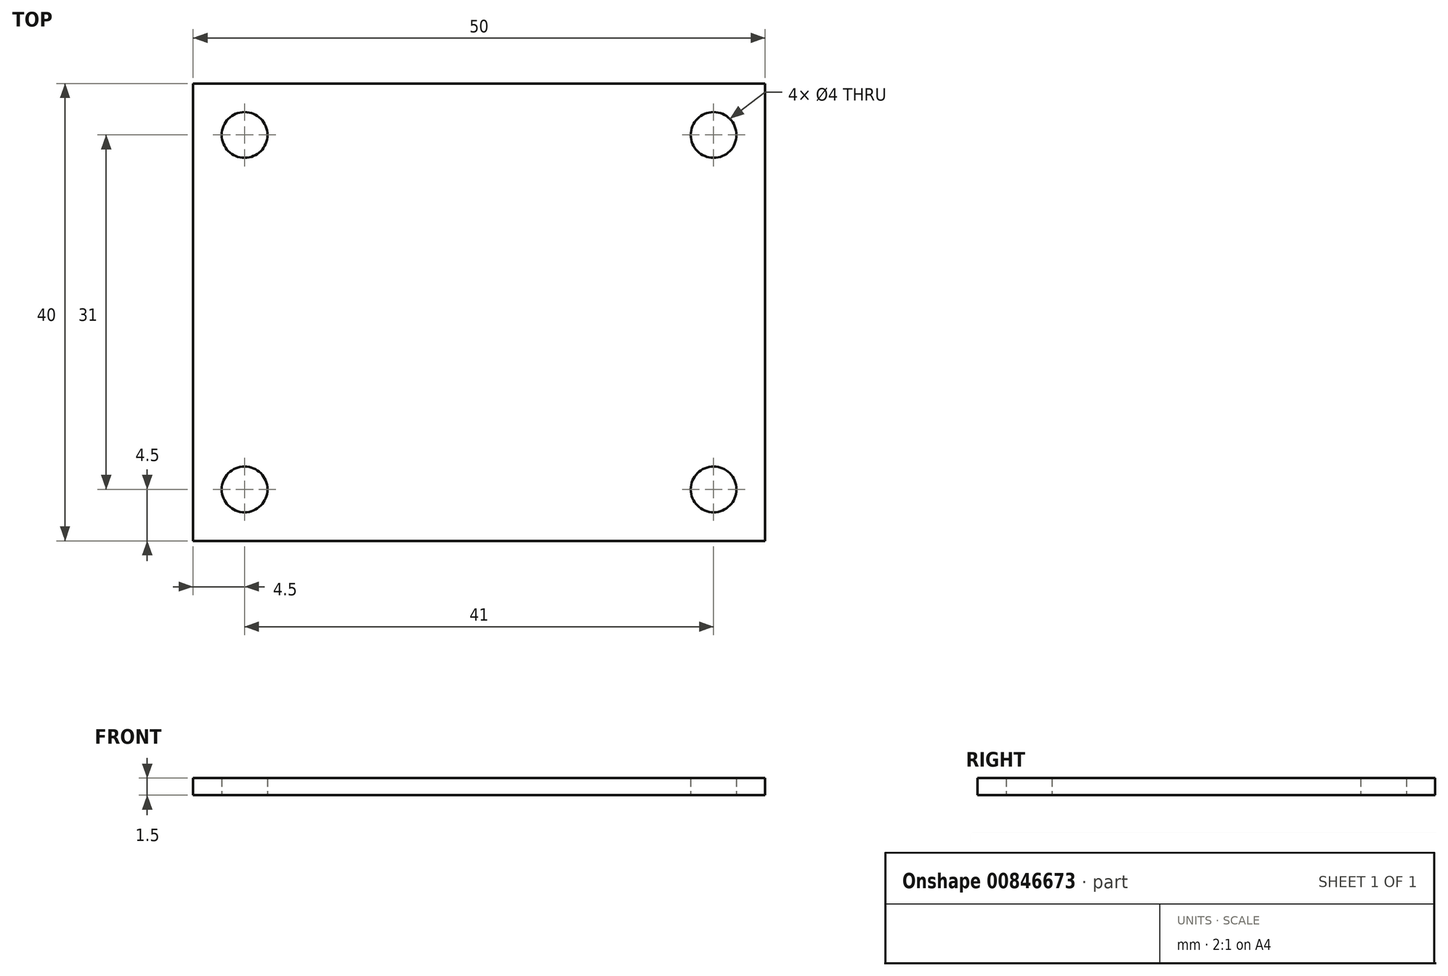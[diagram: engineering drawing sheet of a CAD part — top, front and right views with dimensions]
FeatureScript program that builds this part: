
annotation { "Feature Type Name" : "Feature", "Feature Type Description" : "" }
export const myFeature = defineFeature(function(context is Context, id is Id, definition is map)
    precondition{}
    {
        {
            var Q0;
            Q0=qCreatedBy(makeId("Top.planeOp"),FACE);
            var sketch = newSketch(context, id + "F0", { "sketchPlane" : qUnion([Q0])});
            skLineSegment(sketch, "E0.bottom", {"start": v(-25, 20) * mm, "end": v(25, 20) * mm});
            skLineSegment(sketch, "E0.top", {"start": v(-25, -20) * mm, "end": v(25, -20) * mm});
            skLineSegment(sketch, "E0.left", {"start": v(-25, 20) * mm, "end": v(-25, -20) * mm});
            skLineSegment(sketch, "E0.right", {"start": v(25, 20) * mm, "end": v(25, -20) * mm});
            skCircle(sketch, "E1", {"center": v(-20.5, 15.5) * mm, "radius": 2 * mm});
            skCircle(sketch, "E2", {"center": v(20.5, 15.5) * mm, "radius": 2 * mm});
            skCircle(sketch, "E3", {"center": v(20.5, -15.5) * mm, "radius": 2 * mm});
            skCircle(sketch, "E4", {"center": v(-20.5, -15.5) * mm, "radius": 2 * mm});
            skSolve(sketch);
        }
        {
            var Q0;
            Q0=makeQuery(id+"F0.imprint","IMPRINT",FACE,{"disambiguationData":[TD([[makeQuery(id+"F0.imprint","IMPRINT",EDGE,{"derivedFrom":sQuery(id+"F0.wireOp",EDGE,"E0.bottom")}),-1.0]])]});
            extrude(context, id + "F1", {"entities" : qUnion([Q0]), "depth" : 1.5 * mm, "offsetDistance" : 25 * mm});
        }
    });
